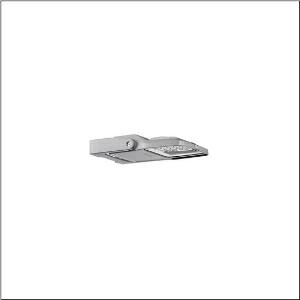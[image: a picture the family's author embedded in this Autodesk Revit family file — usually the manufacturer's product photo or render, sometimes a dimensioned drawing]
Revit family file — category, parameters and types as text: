
# Revit family: floodlight_fl_21_iq_micro___pl61_5xa7761a4c2a_08ca
name_source: partatom
category: Lighting Fixtures
units: mm (PartAtom-declared; Revit-internal decimal feet)

## family parameters
Cut with Voids When Loaded = No
Host = Face
Light Source = No
Part Type = Normal
Room Calculation Point = No
Round Connector Dimension = Use Diameter
Shared = No

## types (1)
- --- (1 x LED, 3030 lm, 23.1 W, 4000K)
    Apparent Load = 23 VA
    CIE Flux Codes = 33 65 98 100 100
    Color Rendering = 70
    Color Temperature = 4000K
    Default Elevation = 1800 mm
    Description = Floodlight FL 21 iQ micro, floodlight, primary light control with lens, of PMMA, primary optical cover: protective disc, of toughened safety glass, transparent, light distribution: PL61, light emission: direct distribution, installation type: surface-mounted, LED, High Power LED, rated luminous flux: 3.030lm, luminous efficacy: 131lm/W, light colour: 740, colour temperature: 4000K, control: optimised constant luminous flux control (CLO 2.0), Desk-Remote (wireless, voltage-free reading and setting of iQ features in the workshop via application-optimized NFC function/RFID function), Light-Fading, Smart-Wire, Night-Set, Lumen-Switch, Temp-Guard, Auto-Match, with terminal, 6-pole, mains connection: 220..240V, AC, 50/60Hz, start of lifetime: 23W, end of service life: 24W, reduction: 11W, luminaire housing, of diecast aluminium, powder-coated, Siteco® metallic grey (DB 702S), corrosivity category C5 mid according to DIN EN ISO 12944, sealing non-destructively replaceable, design bracket, of diecast aluminium, powder-coated, Siteco® metallic grey (DB 702S), protection rating (complete): IP66, insulation class (complete): insulation class II (safety insulation), certification: CE, ENEC, VDE, protection symbol: D, impact resistance: IK07, permissible operating ambient temperature: -40..+40°C, permissible operating ambient temperature for outdoor applications: -40..+50°C, standard: DIN EN 12944, LABS conformity tested according to VDMA 24364:2018-05, packaging unit: 1 piece

Light Distribution: PL61
    Height = 65 mm
    Lamp = 1 x LED
    Lamp Light Flux = 3030 lm
    Lamp Power = 23.1 W
    Lamp count = 1
    Length = 312 mm
    Luminous efficacy = 131 lm/W
    Manufacturer = Siteco
    ModVariant = No
    Model = 5XA7761A4C2A
    Mounting Place = Wall
    Mounting Type = Surface mounted
    Number of Poles = 1
    OnlyDefault = Yes
    Power Factor = 1
    Product Name = Floodlight FL 21 iQ micro | PL61
    Product group = floodlight | wall mounted
    ProductGroupID = 2001
    Protection Class = Protection class II
    Protection Degree = IP 66
    RLX_Detail_Level = 1
    RLX_Emergency_Light_Flux = 0 lm
    RLX_Emergency_Type = 0
    RLX_Emergency_Type_DB = No
    RlxData = <blob elided: 97385 chars, md5=010993a2>
    Socket = socket
    Standby Power = 0 W
    System Light Flux = 3030 lm
    System Power = 23 W
    Type Comments = factory setting: luminous flux: 100 % | dim-lin: 254 | 455 mA
    Type Image = l_1006878.jpg
    URL = http://relux.com
    VarID = @adj_147193
    Voltage = 0 V
    Weight = 0.00 kg
    Width = 230 mm

## geometry (parser evidence)
native form markers: Blend x4, Sweep x14
no freeform markers — native parametric forms only
